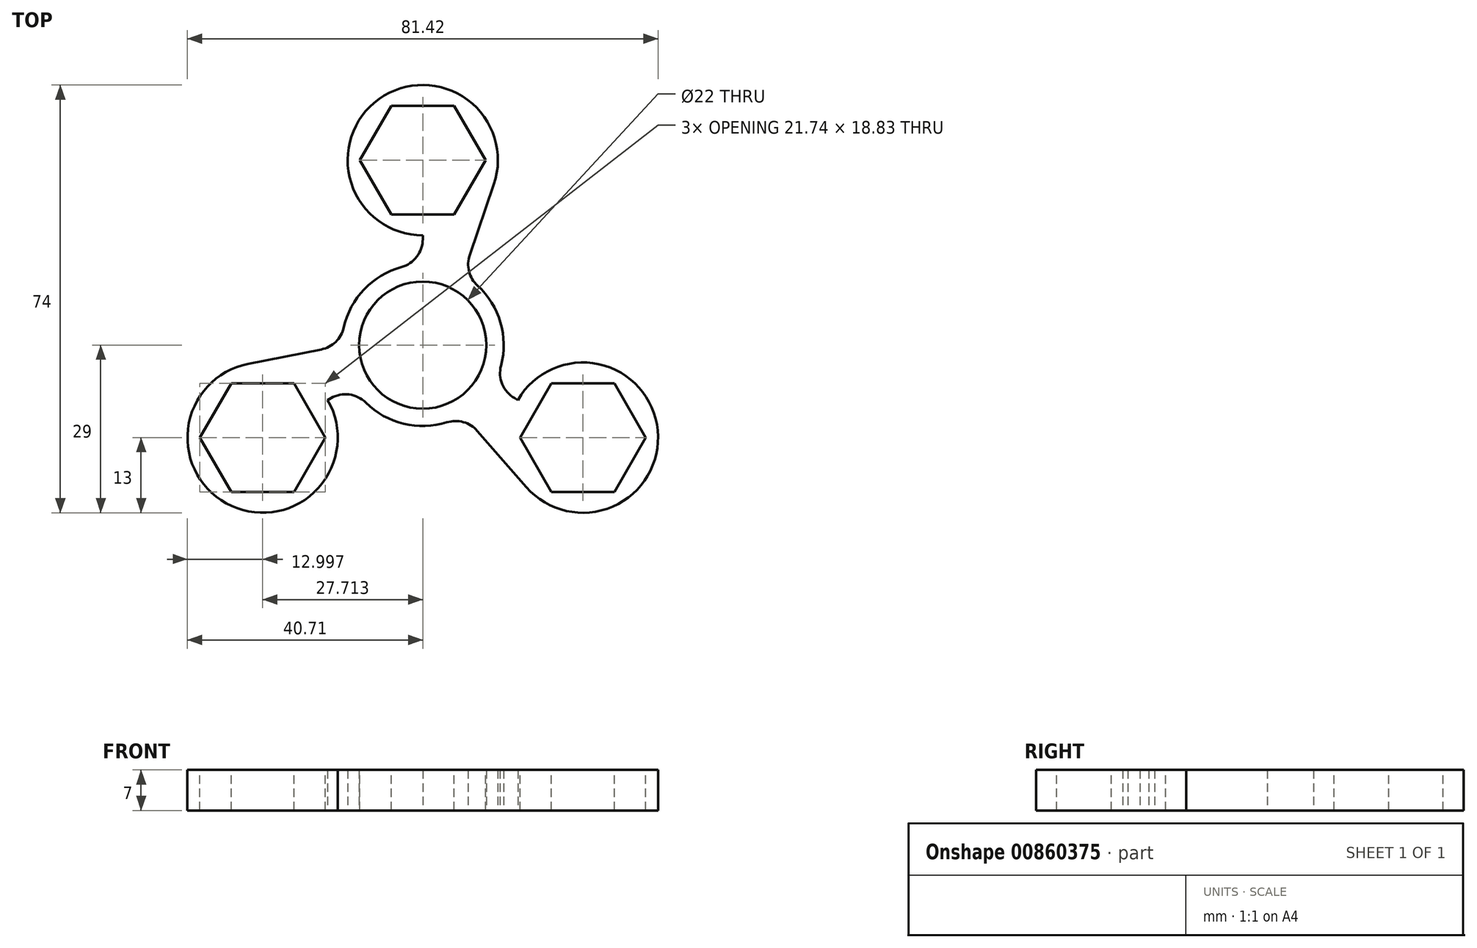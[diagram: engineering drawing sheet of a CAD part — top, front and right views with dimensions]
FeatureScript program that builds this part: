
annotation { "Feature Type Name" : "Feature", "Feature Type Description" : "" }
export const myFeature = defineFeature(function(context is Context, id is Id, definition is map)
    precondition{}
    {
        {
            var Q0;
            Q0=qCreatedBy(makeId("Top.planeOp"),FACE);
            var sketch = newSketch(context, id + "F0", { "sketchPlane" : qUnion([Q0])});
            skCircle(sketch, "E0", {"center": v(0, 0) * mm, "radius": 11 * mm});
            skArc(sketch, "E1.0", {"start": v(0, 14) * mm, "mid": v(-3.6, -13.53) * mm, "end": v(6.95, 12.15) * mm});
            skCircle(sketch, "E2", {"center": v(0, 0) * mm, "radius": 45 * mm, "construction": true});
            skArc(sketch, "E3", {"start": v(12.3, 27.8) * mm, "mid": v(-7.56, 42.58) * mm, "end": v(0, 19) * mm});
            skLineSegment(sketch, "E4", {"start": v(0, 19) * mm, "end": v(0, 14) * mm});
            skLineSegment(sketch, "E5", {"start": v(12.3, 27.8) * mm, "end": v(6.95, 12.15) * mm});
            skPoint(sketch, "E6.orphan", {"position": v(13.74, 32) * mm});
            skArc(sketch, "E7.1.0", {"start": v(-30.22, -3.24) * mm, "mid": v(-33.1, -27.84) * mm, "end": v(-16.45, -9.5) * mm});
            skLineSegment(sketch, "E7.1.1", {"start": v(-30.22, -3.24) * mm, "end": v(-14, -0.05) * mm});
            skLineSegment(sketch, "E7.1.2", {"start": v(-16.45, -9.5) * mm, "end": v(-12.12, -7) * mm});
            skArc(sketch, "E7.2.0", {"start": v(17.92, -24.55) * mm, "mid": v(40.65, -14.74) * mm, "end": v(16.45, -9.5) * mm});
            skLineSegment(sketch, "E7.2.1", {"start": v(17.92, -24.55) * mm, "end": v(7.05, -12.1) * mm});
            skLineSegment(sketch, "E7.2.2", {"start": v(16.45, -9.5) * mm, "end": v(12.12, -7) * mm});
            skSolve(sketch);
        }
        {
            var Q0;
            Q0=makeQuery(id+"F0.imprint","IMPRINT",FACE,{"disambiguationData":[TD([[makeQuery(id+"F0.imprint","IMPRINT",EDGE,{"derivedFrom":sQuery(id+"F0.wireOp",EDGE,"E0")}),-1.0]])]});
            var Q1;
            Q1=makeQuery(id+"F0.imprint","IMPRINT",FACE,{"disambiguationData":[TD([[makeQuery(id+"F0.imprint","IMPRINT",EDGE,{"derivedFrom":sQuery(id+"F0.wireOp",EDGE,"E7.2.0")}),1.0]])]});
            var Q2;
            Q2=makeQuery(id+"F0.imprint","IMPRINT",FACE,{"disambiguationData":[TD([[makeQuery(id+"F0.imprint","IMPRINT",EDGE,{"derivedFrom":sQuery(id+"F0.wireOp",EDGE,"E7.1.0")}),1.0]])]});
            extrude(context, id + "F1", {"entities" : qUnion([Q0, Q1, Q2]), "depth" : 7 * mm, "offsetDistance" : 25 * mm});
        }
        {
            var Q0;
            Q0=makeQuery(id+"F1.opExtrude","CAP_FACE",FACE,{"disambiguationData":[OSD([sQuery(id+"F0.wireOp",EDGE,"E0"),sQuery(id+"F0.wireOp",EDGE,"E1.0"),sQuery(id+"F0.wireOp",EDGE,"E3"),sQuery(id+"F0.wireOp",EDGE,"E4"),sQuery(id+"F0.wireOp",EDGE,"E5"),sQuery(id+"F0.wireOp",EDGE,"E7.1.0"),sQuery(id+"F0.wireOp",EDGE,"E7.1.1"),sQuery(id+"F0.wireOp",EDGE,"E7.1.2"),sQuery(id+"F0.wireOp",EDGE,"E7.2.0"),sQuery(id+"F0.wireOp",EDGE,"E7.2.1"),sQuery(id+"F0.wireOp",EDGE,"E7.2.2")])],"isStart":false});
            var sketch = newSketch(context, id + "F2", { "sketchPlane" : qUnion([Q0])});
            skCircle(sketch, "E8.cCircle", {"center": v(0, 32) * mm, "radius": 9.41 * mm, "construction": true});
            skLineSegment(sketch, "E8.0", {"start": v(-5.44, 41.41) * mm, "end": v(5.44, 41.41) * mm});
            skLineSegment(sketch, "E8.1", {"start": v(5.44, 41.41) * mm, "end": v(10.87, 32) * mm});
            skLineSegment(sketch, "E8.2", {"start": v(10.87, 32) * mm, "end": v(5.44, 22.59) * mm});
            skLineSegment(sketch, "E8.3", {"start": v(5.44, 22.59) * mm, "end": v(-5.44, 22.59) * mm});
            skLineSegment(sketch, "E8.4", {"start": v(-5.44, 22.58) * mm, "end": v(-10.87, 32) * mm});
            skLineSegment(sketch, "E8.5", {"start": v(-10.87, 32) * mm, "end": v(-5.44, 41.41) * mm});
            skPoint(sketch, "E8.0.midPoint", {"position": v(0, 41.41) * mm});
            skLineSegment(sketch, "E9.1.0", {"start": v(-33.15, -6.58) * mm, "end": v(-22.28, -6.58) * mm});
            skLineSegment(sketch, "E9.1.1", {"start": v(-38.58, -16) * mm, "end": v(-33.15, -6.58) * mm});
            skLineSegment(sketch, "E9.1.2", {"start": v(-33.15, -25.41) * mm, "end": v(-38.58, -16) * mm});
            skLineSegment(sketch, "E9.1.3", {"start": v(-22.28, -25.41) * mm, "end": v(-33.15, -25.41) * mm});
            skLineSegment(sketch, "E9.1.4", {"start": v(-16.84, -16) * mm, "end": v(-22.28, -25.41) * mm});
            skLineSegment(sketch, "E9.1.5", {"start": v(-22.28, -6.58) * mm, "end": v(-16.84, -16) * mm});
            skLineSegment(sketch, "E9.2.0", {"start": v(22.28, -25.42) * mm, "end": v(16.84, -16) * mm});
            skLineSegment(sketch, "E9.2.1", {"start": v(33.15, -25.42) * mm, "end": v(22.28, -25.42) * mm});
            skLineSegment(sketch, "E9.2.2", {"start": v(38.58, -16) * mm, "end": v(33.15, -25.42) * mm});
            skLineSegment(sketch, "E9.2.3", {"start": v(33.15, -6.59) * mm, "end": v(38.58, -16) * mm});
            skLineSegment(sketch, "E9.2.4", {"start": v(22.28, -6.59) * mm, "end": v(33.15, -6.59) * mm});
            skLineSegment(sketch, "E9.2.5", {"start": v(16.84, -16) * mm, "end": v(22.28, -6.59) * mm});
            skPoint(sketch, "E9.center", {"position": v(0, 0) * mm});
            skSolve(sketch);
        }
        {
            var Q0;
            Q0=makeQuery(id+"F2.imprint","IMPRINT",FACE,{"disambiguationData":[TD([[makeQuery(id+"F2.imprint","IMPRINT",EDGE,{"derivedFrom":sQuery(id+"F2.wireOp",EDGE,"E8.0")}),-1.0]])]});
            var Q1;
            Q1=makeQuery(id+"F2.imprint","IMPRINT",FACE,{"disambiguationData":[TD([[makeQuery(id+"F2.imprint","IMPRINT",EDGE,{"derivedFrom":sQuery(id+"F2.wireOp",EDGE,"E9.2.0")}),-1.0]])]});
            var Q2;
            Q2=makeQuery(id+"F2.imprint","IMPRINT",FACE,{"disambiguationData":[TD([[makeQuery(id+"F2.imprint","IMPRINT",EDGE,{"derivedFrom":sQuery(id+"F2.wireOp",EDGE,"E9.1.0")}),-1.0]])]});
            extrude(context, id + "F3", {"entities" : qUnion([Q0, Q1, Q2]), "operationType" : NewBodyOperationType.REMOVE, "oppositeDirection" : true, "depth" : 25 * mm, "offsetDistance" : 25 * mm});
        }
        {
            var Q0;
            Q0=makeQuery(id+"F1.opExtrude","SWEPT_EDGE",EDGE,{"disambiguationData":[OSD([sQuery(id+"F0.wireOp",EDGE,"E1.0"),sQuery(id+"F0.wireOp",EDGE,"E5")])]});
            var Q1;
            Q1=makeQuery(id+"F1.opExtrude","SWEPT_EDGE",EDGE,{"disambiguationData":[OSD([sQuery(id+"F0.wireOp",EDGE,"E1.0"),sQuery(id+"F0.wireOp",EDGE,"E7.2.2")])]});
            var Q2;
            Q2=makeQuery(id+"F1.opExtrude","SWEPT_EDGE",EDGE,{"disambiguationData":[OSD([sQuery(id+"F0.wireOp",EDGE,"E1.0"),sQuery(id+"F0.wireOp",EDGE,"E7.2.1")])]});
            var Q3;
            Q3=makeQuery(id+"F1.opExtrude","SWEPT_EDGE",EDGE,{"disambiguationData":[OSD([sQuery(id+"F0.wireOp",EDGE,"E1.0"),sQuery(id+"F0.wireOp",EDGE,"E7.1.2")])]});
            var Q4;
            Q4=makeQuery(id+"F1.opExtrude","SWEPT_EDGE",EDGE,{"disambiguationData":[OSD([sQuery(id+"F0.wireOp",EDGE,"E1.0"),sQuery(id+"F0.wireOp",EDGE,"E7.1.1")])]});
            var Q5;
            Q5=makeQuery(id+"F1.opExtrude","SWEPT_EDGE",EDGE,{"disambiguationData":[OSD([sQuery(id+"F0.wireOp",EDGE,"E1.0"),sQuery(id+"F0.wireOp",EDGE,"E4")])]});
            fillet(context, id + "F4", {"entities" : qUnion([Q0, Q1, Q2, Q3, Q4, Q5]), "radius" : 5 * mm, "tangentPropagation" : true, "allowEdgeOverflow" : false});
        }
    });
